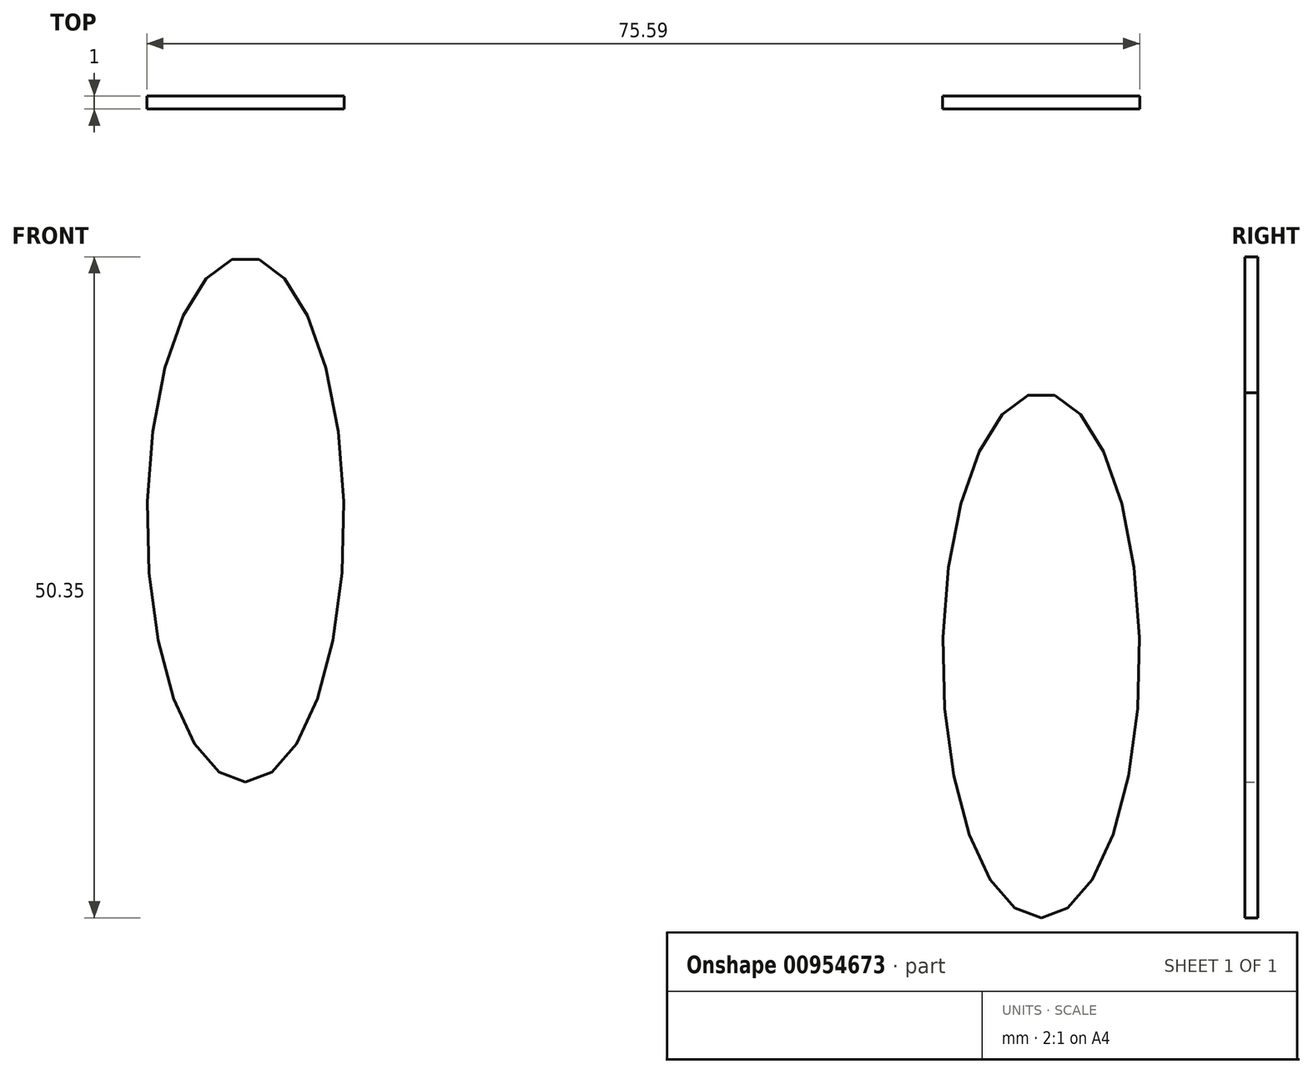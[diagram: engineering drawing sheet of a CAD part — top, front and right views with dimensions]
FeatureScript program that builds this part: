
annotation { "Feature Type Name" : "Feature", "Feature Type Description" : "" }
export const myFeature = defineFeature(function(context is Context, id is Id, definition is map)
    precondition{}
    {
        {
            var Q0;
            Q0=qCreatedBy(makeId("Front.planeOp"),FACE);
            var sketch = newSketch(context, id + "F0", { "sketchPlane" : qUnion([Q0])});
            skEllipse(sketch, "E0", {"center": v(0, 0) * mm, "majorRadius": 20 * mm, "minorRadius": 7.5 * mm, "majorAxis": v(0, -1)});
            skSolve(sketch);
        }
        {
            var Q0;
            Q0=makeQuery(id+"F0.imprint","IMPRINT",FACE,{"disambiguationData":[TD([[makeQuery(id+"F0.imprint","IMPRINT",EDGE,{"derivedFrom":sQuery(id+"F0.wireOp",EDGE,"E0")}),1.0]])]});
            extrude(context, id + "F1", {"entities" : qUnion([Q0]), "depth" : 1 * mm, "offsetDistance" : 25.4 * mm});
        }
        {
            var Q0;
            Q0=qCreatedBy(makeId("Front.planeOp"),FACE);
            var sketch = newSketch(context, id + "F2", { "sketchPlane" : qUnion([Q0])});
            skEllipse(sketch, "E1", {"center": v(-60.59, 10.35) * mm, "majorRadius": 20 * mm, "minorRadius": 7.5 * mm, "majorAxis": v(0, -1)});
            skSolve(sketch);
        }
        {
            var Q0;
            Q0=makeQuery(id+"F2.imprint","IMPRINT",FACE,{"disambiguationData":[TD([[makeQuery(id+"F2.imprint","IMPRINT",EDGE,{"derivedFrom":sQuery(id+"F2.wireOp",EDGE,"E1")}),1.0]])]});
            extrude(context, id + "F3", {"entities" : qUnion([Q0]), "depth" : 1 * mm, "offsetDistance" : 25.4 * mm});
        }
    });
